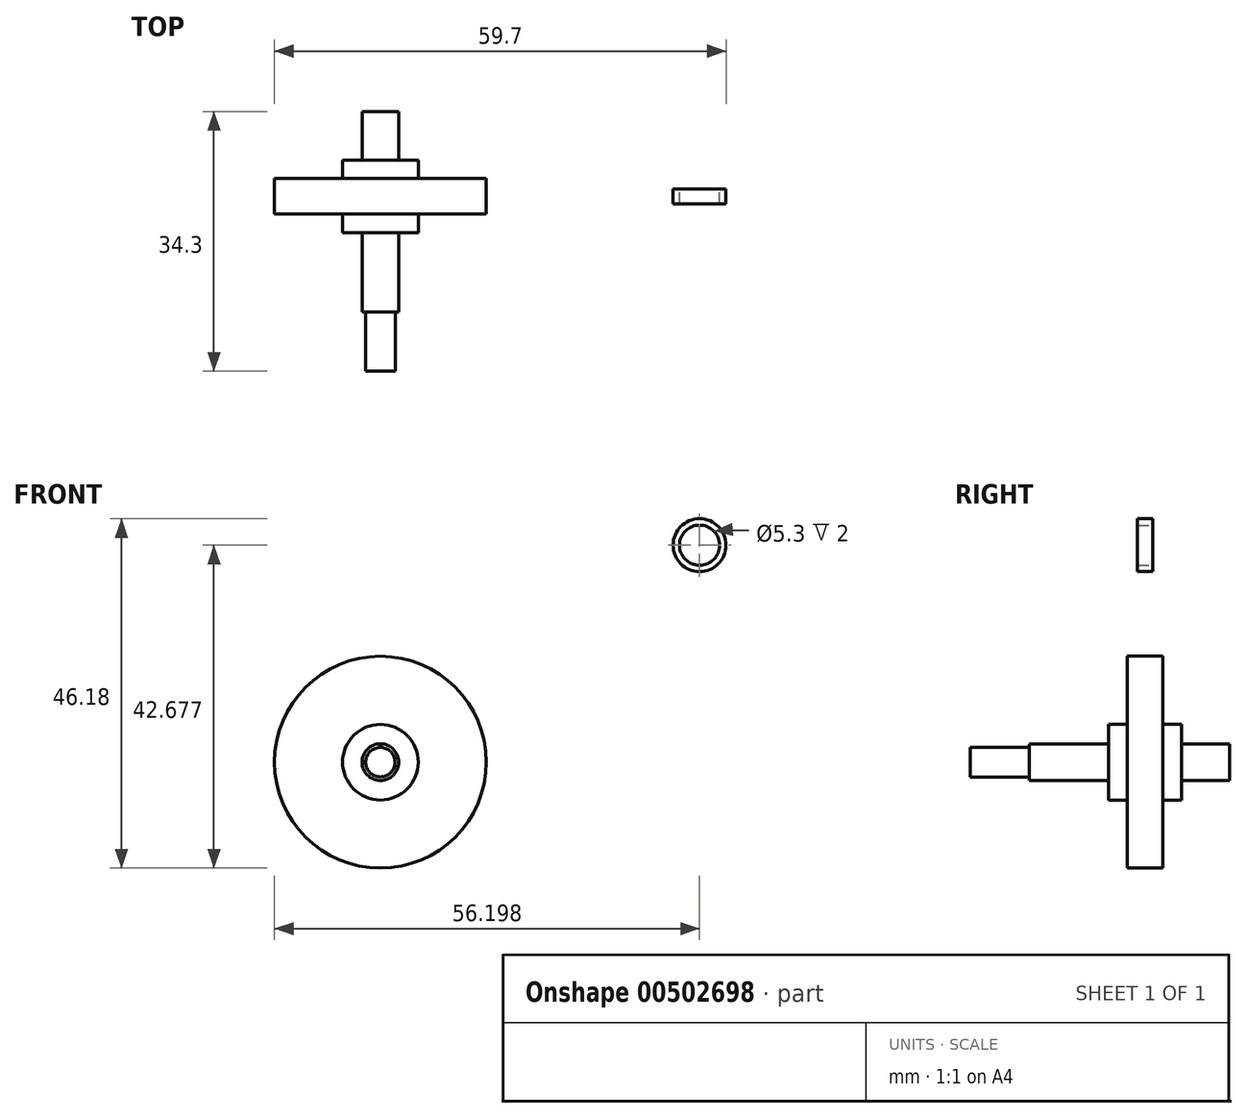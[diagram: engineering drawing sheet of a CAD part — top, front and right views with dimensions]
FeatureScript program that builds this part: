
annotation { "Feature Type Name" : "Feature", "Feature Type Description" : "" }
export const myFeature = defineFeature(function(context is Context, id is Id, definition is map)
    precondition{}
    {
        {
            var Q0;
            Q0=qCreatedBy(makeId("Front.planeOp"),FACE);
            var sketch = newSketch(context, id + "F0", { "sketchPlane" : qUnion([Q0])});
            skCircle(sketch, "E0", {"center": v(0, 0) * mm, "radius": 14 * mm});
            skSolve(sketch);
        }
        {
            var Q0;
            Q0 = qSketchRegion(id + "F0", true);
            extrude(context, id + "F1", {"entities" : qUnion([Q0]), "endBound" : BoundingType.SYMMETRIC, "depth" : 4.7 * mm});
        }
        {
            var Q0;
            Q0=qCreatedBy(makeId("Front.planeOp"),FACE);
            var sketch = newSketch(context, id + "F2", { "sketchPlane" : qUnion([Q0])});
            skCircle(sketch, "E1", {"center": v(0, 0) * mm, "radius": 5 * mm});
            skSolve(sketch);
        }
        {
            var Q0;
            Q0 = qSketchRegion(id + "F2", true);
            extrude(context, id + "F3", {"entities" : qUnion([Q0]), "operationType" : NewBodyOperationType.ADD, "endBound" : BoundingType.SYMMETRIC, "depth" : 9.6 * mm});
        }
        {
            var Q0;
            Q0=makeQuery(id+"F3.opExtrude","CAP_FACE",FACE,{"disambiguationData":[OSD([sQuery(id+"F2.wireOp",EDGE,"E1")])],"isStart":false});
            var sketch = newSketch(context, id + "F4", { "sketchPlane" : qUnion([Q0])});
            skCircle(sketch, "E2", {"center": v(0, 0) * mm, "radius": 2.43 * mm});
            skSolve(sketch);
        }
        {
            var Q0;
            Q0 = qSketchRegion(id + "F4", true);
            extrude(context, id + "F5", {"entities" : qUnion([Q0]), "operationType" : NewBodyOperationType.ADD, "depth" : 10.5 * mm, "hasSecondDirection" : true, "secondDirectionOppositeDirection" : true, "secondDirectionDepth" : 16 * mm});
        }
        {
            var Q0;
            Q0=makeQuery(id+"F5.opExtrude","CAP_FACE",FACE,{"disambiguationData":[OSD([sQuery(id+"F4.wireOp",EDGE,"E2")])],"isStart":false});
            var sketch = newSketch(context, id + "F6", { "sketchPlane" : qUnion([Q0])});
            skCircle(sketch, "E3", {"center": v(0, 0) * mm, "radius": 1.95 * mm});
            skSolve(sketch);
        }
        {
            var Q0;
            Q0 = qSketchRegion(id + "F6", true);
            extrude(context, id + "F7", {"entities" : qUnion([Q0]), "operationType" : NewBodyOperationType.ADD, "depth" : 7.8 * mm});
        }
        {
            var Q0;
            Q0=qCreatedBy(makeId("Front.planeOp"),FACE);
            var sketch = newSketch(context, id + "F8", { "sketchPlane" : qUnion([Q0])});
            skCircle(sketch, "E4", {"center": v(42.2, 28.68) * mm, "radius": 2.65 * mm});
            skCircle(sketch, "E5", {"center": v(42.2, 28.68) * mm, "radius": 3.5 * mm});
            skSolve(sketch);
        }
        {
            var Q0;
            Q0 = qSketchRegion(id + "F8", true);
            extrude(context, id + "F9", {"entities" : qUnion([Q0]), "depth" : 1 * mm});
        }
        {
            var Q0;
            Q0=makeQuery(id+"F9.opExtrude","CAP_FACE",FACE,{"disambiguationData":[OSD([sQuery(id+"F8.wireOp",EDGE,"E4"),sQuery(id+"F8.wireOp",EDGE,"E5")])],"isStart":true});
            var sketch = newSketch(context, id + "F10", { "sketchPlane" : qUnion([Q0])});
            skCircle(sketch, "E6", {"center": v(-42.2, 28.68) * mm, "radius": 2.65 * mm});
            skCircle(sketch, "E7", {"center": v(-42.2, 28.68) * mm, "radius": 3.5 * mm});
            skSolve(sketch);
        }
        {
            var Q0;
            Q0 = qSketchRegion(id + "F10", true);
            extrude(context, id + "F11", {"entities" : qUnion([Q0]), "operationType" : NewBodyOperationType.ADD, "depth" : 1 * mm});
        }
    });
